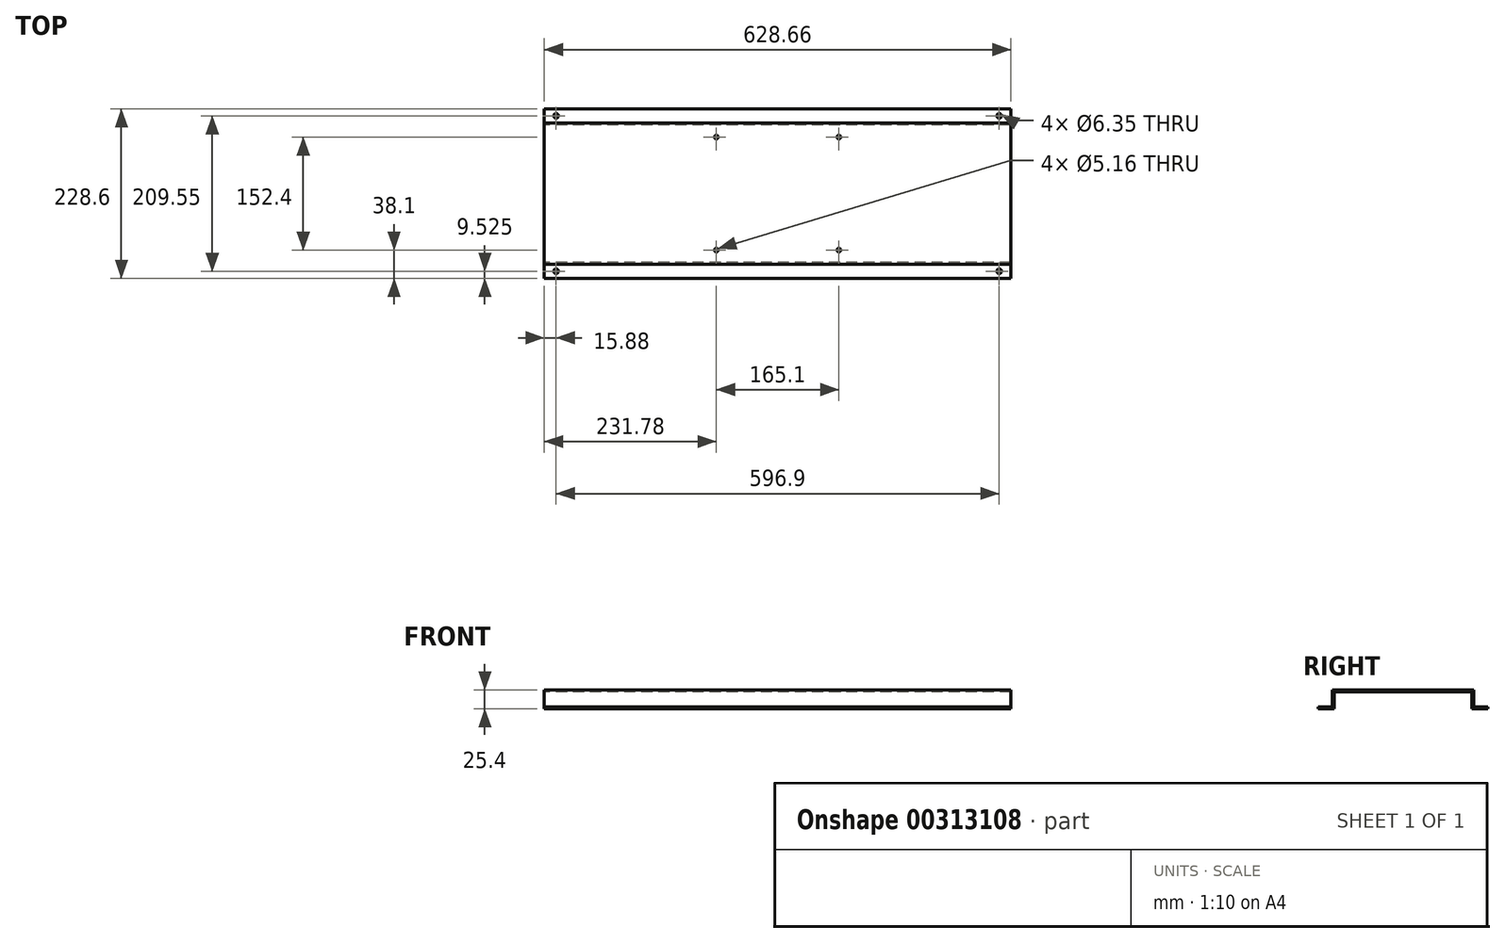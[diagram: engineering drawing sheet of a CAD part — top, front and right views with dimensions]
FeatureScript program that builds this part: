
annotation { "Feature Type Name" : "Feature", "Feature Type Description" : "" }
export const myFeature = defineFeature(function(context is Context, id is Id, definition is map)
    precondition{}
    {
        {
            var Q0;
            Q0=qCreatedBy(makeId("Right.planeOp"),FACE);
            var sketch = newSketch(context, id + "F0", { "sketchPlane" : qUnion([Q0])});
            skLineSegment(sketch, "E0", {"start": v(-114.3, 0) * mm, "end": v(-92.63, 0) * mm});
            skLineSegment(sketch, "E1", {"start": v(-92.63, 0) * mm, "end": v(-92.63, 22.86) * mm});
            skLineSegment(sketch, "E2", {"start": v(-92.63, 22.86) * mm, "end": v(92.63, 22.86) * mm});
            skLineSegment(sketch, "E3", {"start": v(92.63, 22.86) * mm, "end": v(92.63, 0) * mm});
            skLineSegment(sketch, "E4", {"start": v(92.63, 0) * mm, "end": v(114.3, 0) * mm});
            skLineSegment(sketch, "E5", {"start": v(114.3, 0) * mm, "end": v(114.3, 2.54) * mm});
            skLineSegment(sketch, "E6", {"start": v(114.3, 2.54) * mm, "end": v(95.17, 2.54) * mm});
            skLineSegment(sketch, "E7", {"start": v(95.17, 2.54) * mm, "end": v(95.17, 25.4) * mm});
            skLineSegment(sketch, "E8", {"start": v(95.17, 25.4) * mm, "end": v(-95.17, 25.4) * mm});
            skLineSegment(sketch, "E9", {"start": v(-95.17, 25.4) * mm, "end": v(-95.17, 2.54) * mm});
            skLineSegment(sketch, "E10", {"start": v(-95.17, 2.54) * mm, "end": v(-114.3, 2.54) * mm});
            skLineSegment(sketch, "E11", {"start": v(-114.3, 2.54) * mm, "end": v(-114.3, 0) * mm});
            skPoint(sketch, "E12", {"position": v(0, 25.4) * mm});
            skSolve(sketch);
        }
        {
            var Q0;
            Q0 = qSketchRegion(id + "F0", true);
            extrude(context, id + "F1", {"entities" : qUnion([Q0]), "endBound" : BoundingType.SYMMETRIC, "depth" : 628.65 * mm, "offsetDistance" : 25.4 * mm});
        }
        {
            var Q0;
            Q0=makeQuery(id+"F1.opExtrude","SWEPT_FACE",FACE,{"disambiguationData":[OSD([sQuery(id+"F0.wireOp",EDGE,"E8")])]});
            var sketch = newSketch(context, id + "F2", { "sketchPlane" : qUnion([Q0])});
            skLineSegment(sketch, "E13.bottom", {"start": v(82.55, 76.2) * mm, "end": v(-82.55, 76.2) * mm, "construction": true});
            skLineSegment(sketch, "E13.top", {"start": v(82.55, -76.2) * mm, "end": v(-82.55, -76.2) * mm, "construction": true});
            skLineSegment(sketch, "E13.left", {"start": v(82.55, 76.2) * mm, "end": v(82.55, -76.2) * mm, "construction": true});
            skLineSegment(sketch, "E13.right", {"start": v(-82.55, 76.2) * mm, "end": v(-82.55, -76.2) * mm, "construction": true});
            skPoint(sketch, "E13.middle", {"position": v(0, 0) * mm});
            skPoint(sketch, "E13.middle.positionSnap0", {"position": v(0, 95.17) * mm});
            skPoint(sketch, "E13.middle.positionSnap1", {"position": v(-314.33, 0) * mm});
            skPoint(sketch, "E13.centerSnap0", {"position": v(0, 95.17) * mm});
            skPoint(sketch, "E13.centerSnap1", {"position": v(-314.33, 0) * mm});
            skCircle(sketch, "E14", {"center": v(-82.55, 76.2) * mm, "radius": 2.58 * mm});
            skCircle(sketch, "E15", {"center": v(-82.55, -76.2) * mm, "radius": 2.58 * mm});
            skCircle(sketch, "E16", {"center": v(82.55, -76.2) * mm, "radius": 2.58 * mm});
            skCircle(sketch, "E17", {"center": v(82.55, 76.2) * mm, "radius": 2.58 * mm});
            skLineSegment(sketch, "E18.bottom", {"start": v(298.45, 104.78) * mm, "end": v(-298.45, 104.78) * mm, "construction": true});
            skLineSegment(sketch, "E18.top", {"start": v(298.45, -104.78) * mm, "end": v(-298.45, -104.78) * mm, "construction": true});
            skLineSegment(sketch, "E18.left", {"start": v(298.45, 104.78) * mm, "end": v(298.45, -104.78) * mm, "construction": true});
            skLineSegment(sketch, "E18.right", {"start": v(-298.45, 104.78) * mm, "end": v(-298.45, -104.78) * mm, "construction": true});
            skCircle(sketch, "E19", {"center": v(298.45, 104.78) * mm, "radius": 3.18 * mm});
            skCircle(sketch, "E20", {"center": v(298.45, -104.78) * mm, "radius": 3.18 * mm});
            skCircle(sketch, "E21", {"center": v(-298.45, -104.78) * mm, "radius": 3.18 * mm});
            skCircle(sketch, "E22", {"center": v(-298.45, 104.78) * mm, "radius": 3.18 * mm});
            skSolve(sketch);
        }
        {
            var Q0;
            Q0 = qSketchRegion(id + "F2", true);
            extrude(context, id + "F3", {"entities" : qUnion([Q0]), "operationType" : NewBodyOperationType.REMOVE, "endBound" : BoundingType.THROUGH_ALL, "oppositeDirection" : true, "depth" : 25.4 * mm, "offsetDistance" : 25.4 * mm});
        }
    });
